# Revit family: Shower_Wall_Nero_Mecca
name_source: partatom
category: Plumbing Fixtures
units: mm (PartAtom-declared; Revit-internal decimal feet)

## family parameters
Always vertical = Yes
Cut with Voids When Loaded = Yes
Maintain Annotation Orientation = No
OmniClass Number = 23.31.17.00
Part Type = Normal
Room Calculation Point = No
Round Connector Dimension = Use Diameter
Shared = No
Work Plane-Based = No

## types (5) — shared parameters
Assembly Code = D2010710
CW Connection = Yes
HW Connection = Yes
IfcExportAs = IfcSanitaryTerminal
IfcExportType = SHOWER
Manufacturer = Nero
ManufacturerOverallDepth = 500 mm  [stored 1.64042 ft]
ManufacturerOverallHeight = 410 mm
ManufacturerOverallWidth = 250 mm
ManufacturerURLProductSpecific = https://nerotapware.com.au
ModifiedIssue = 20241210 $
URL = https://nerotapware.com.au
Uniclass2015Code = Pr_40_20_87_75
Uniclass2015Title = Shower fittings package
Uniclass2015Version = Products v1.35
Vent Connection = No
Waste Connection = No
zero-valued in all types: Default Elevation

## per-type parameters (varying)
| type | BodyMaterial | Description | ManufacturerSpecCode | Model | Type Comments |
| Chrome (NR250805eCH) | Metal_Chrome_Nero | Mecca 2 In 1 Twin Shower Chrome | NR250805eCH | NR250805eCH | Shower - Wall - Chrome |
| Matte Black (NR250805eMB) | Metal_MatteBlack_Nero | Mecca 2 In 1 Twin Shower Matte Black | NR250805eMB | NR250805eMB | Shower - Wall - Matte Black |
| Brushed Nickel (NR250805eBN) | Metal_Nickel_Nero_Brushed | Mecca 2 In 1 Twin Shower Brushed Nickel | NR250805eBN | NR250805eBN | Shower - Wall - Brushed Nickel |
| Gun Metal (NR250805eGM) | Metal_GunMetal_Nero | Mecca 2 In 1 Twin Shower Gun Metal | NR250805eGM | NR250805eGM | Shower - Wall - Gun Metal |
| Brushed Gold (NR250805eBG) | Metal_Gold_Nero_Brushed | Mecca 2 In 1 Twin Shower Brushed Gold | NR250805eBG | NR250805eBG | Shower - Wall - Brushed Gold |

note: [stored X ft] marks values corroborated as IEEE doubles in the binary element streams (Revit-internal decimal feet)

## geometry (parser evidence)
native form markers: Sweep x2
no freeform markers — native parametric forms only
